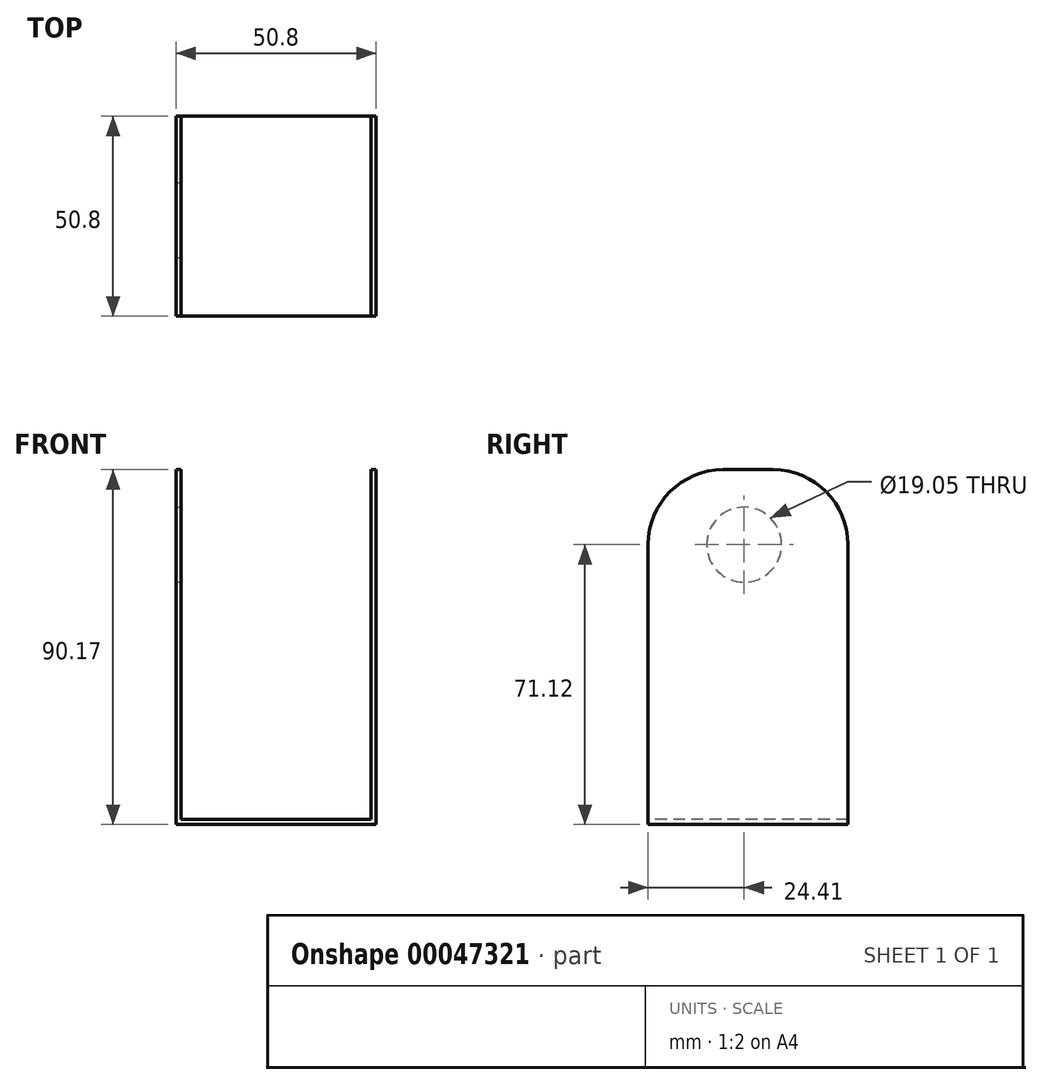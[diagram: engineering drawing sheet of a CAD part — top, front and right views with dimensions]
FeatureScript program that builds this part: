
annotation { "Feature Type Name" : "Feature", "Feature Type Description" : "" }
export const myFeature = defineFeature(function(context is Context, id is Id, definition is map)
    precondition{}
    {
        {
            var Q0;
            Q0=qCreatedBy(makeId("Top.planeOp"),FACE);
            var sketch = newSketch(context, id + "F0", { "sketchPlane" : qUnion([Q0])});
            skLineSegment(sketch, "E0.bottom", {"start": v(-21.49, 26.4) * mm, "end": v(29.31, 26.4) * mm});
            skLineSegment(sketch, "E0.top", {"start": v(-21.49, -24.4) * mm, "end": v(29.31, -24.4) * mm});
            skLineSegment(sketch, "E0.left", {"start": v(-21.49, 26.4) * mm, "end": v(-21.49, -24.4) * mm});
            skLineSegment(sketch, "E0.right", {"start": v(29.31, 26.4) * mm, "end": v(29.31, -24.4) * mm});
            skSolve(sketch);
        }
        {
            var Q0;
            Q0=makeQuery(id+"F0.imprint","IMPRINT",FACE,{"disambiguationData":[TD([[makeQuery(id+"F0.imprint","IMPRINT",EDGE,{"derivedFrom":sQuery(id+"F0.wireOp",EDGE,"E0.bottom")}),-1.0]])]});
            extrude(context, id + "F1", {"entities" : qUnion([Q0]), "depth" : 1.27 * mm});
        }
        {
            var Q0;
            Q0=makeQuery(id+"F1.opExtrude","CAP_FACE",FACE,{"disambiguationData":[OSD([sQuery(id+"F0.wireOp",EDGE,"E0.bottom"),sQuery(id+"F0.wireOp",EDGE,"E0.top"),sQuery(id+"F0.wireOp",EDGE,"E0.left"),sQuery(id+"F0.wireOp",EDGE,"E0.right")])],"isStart":false});
            var sketch = newSketch(context, id + "F2", { "sketchPlane" : qUnion([Q0])});
            skLineSegment(sketch, "E1.bottom", {"start": v(-21.49, 26.4) * mm, "end": v(-20.22, 26.4) * mm});
            skLineSegment(sketch, "E1.top", {"start": v(-21.49, -24.4) * mm, "end": v(-20.22, -24.4) * mm});
            skLineSegment(sketch, "E1.left", {"start": v(-21.49, 26.4) * mm, "end": v(-21.49, -24.4) * mm});
            skLineSegment(sketch, "E1.right", {"start": v(-20.22, 26.4) * mm, "end": v(-20.22, -24.4) * mm});
            skLineSegment(sketch, "E2.bottom", {"start": v(28.04, 26.4) * mm, "end": v(29.31, 26.4) * mm});
            skLineSegment(sketch, "E2.top", {"start": v(28.04, -24.4) * mm, "end": v(29.31, -24.4) * mm});
            skLineSegment(sketch, "E2.left", {"start": v(28.04, 26.4) * mm, "end": v(28.04, -24.4) * mm});
            skLineSegment(sketch, "E2.right", {"start": v(29.31, 26.4) * mm, "end": v(29.31, -24.4) * mm});
            skSolve(sketch);
        }
        {
            var Q0;
            Q0=makeQuery(id+"F2.imprint","IMPRINT",FACE,{"disambiguationData":[TD([[makeQuery(id+"F2.imprint","IMPRINT",EDGE,{"derivedFrom":sQuery(id+"F2.wireOp",EDGE,"E1.bottom")}),-1.0]])]});
            var Q1;
            Q1=makeQuery(id+"F2.imprint","IMPRINT",FACE,{"disambiguationData":[TD([[makeQuery(id+"F2.imprint","IMPRINT",EDGE,{"derivedFrom":sQuery(id+"F2.wireOp",EDGE,"E2.bottom")}),-1.0]])]});
            extrude(context, id + "F3", {"entities" : qUnion([Q0, Q1]), "operationType" : NewBodyOperationType.ADD, "depth" : 88.9 * mm});
        }
        {
            var Q0;
            Q0=makeQuery(id+"F3.opExtrude","CAP_EDGE",EDGE,{"disambiguationData":[OSD([sQuery(id+"F2.wireOp",EDGE,"E2.bottom")])],"isStart":false});
            var Q1;
            Q1=makeQuery(id+"F3.opExtrude","CAP_EDGE",EDGE,{"disambiguationData":[OSD([sQuery(id+"F2.wireOp",EDGE,"E1.bottom")])],"isStart":false});
            fillet(context, id + "F4", {"entities" : qUnion([Q0, Q1]), "radius" : 19.05 * mm, "tangentPropagation" : true, "allowEdgeOverflow" : false});
        }
        {
            var Q0;
            Q0=makeQuery(id+"F3.opExtrude","CAP_EDGE",EDGE,{"disambiguationData":[OSD([sQuery(id+"F2.wireOp",EDGE,"E1.top")])],"isStart":false});
            var Q1;
            Q1=makeQuery(id+"F3.opExtrude","CAP_EDGE",EDGE,{"disambiguationData":[OSD([sQuery(id+"F2.wireOp",EDGE,"E2.top")])],"isStart":false});
            fillet(context, id + "F5", {"entities" : qUnion([Q0, Q1]), "radius" : 19.05 * mm, "tangentPropagation" : true, "allowEdgeOverflow" : false});
        }
        {
            var Q0;
            Q0=makeQuery(id+"F3.opExtrude","SWEPT_FACE",FACE,{"disambiguationData":[OSD([sQuery(id+"F2.wireOp",EDGE,"E1.right")])]});
            var sketch = newSketch(context, id + "F6", { "sketchPlane" : qUnion([Q0])});
            skCircle(sketch, "E3", {"center": v(0, 71.12) * mm, "radius": 9.53 * mm});
            skSolve(sketch);
        }
        {
            var Q0;
            Q0=sQuery(id+"F6.wireOp",VERTEX,"E3.center");
            var Q1;
            Q1=makeQuery(id+"F1.opExtrude","SWEPT_BODY",BODY,{"disambiguationData":[OSD([sQuery(id+"F0.wireOp",EDGE,"E0.bottom"),sQuery(id+"F0.wireOp",EDGE,"E0.top"),sQuery(id+"F0.wireOp",EDGE,"E0.left"),sQuery(id+"F0.wireOp",EDGE,"E0.right")])]});
            hole(context, id + "F7", {"style" : HoleStyle.SIMPLE, "holeDiameter" : 19.05 * mm, "endStyle" : HoleEndStyle.THROUGH, "locations" : qUnion([Q0]), "scope" : qUnion([Q1])});
        }
    });
